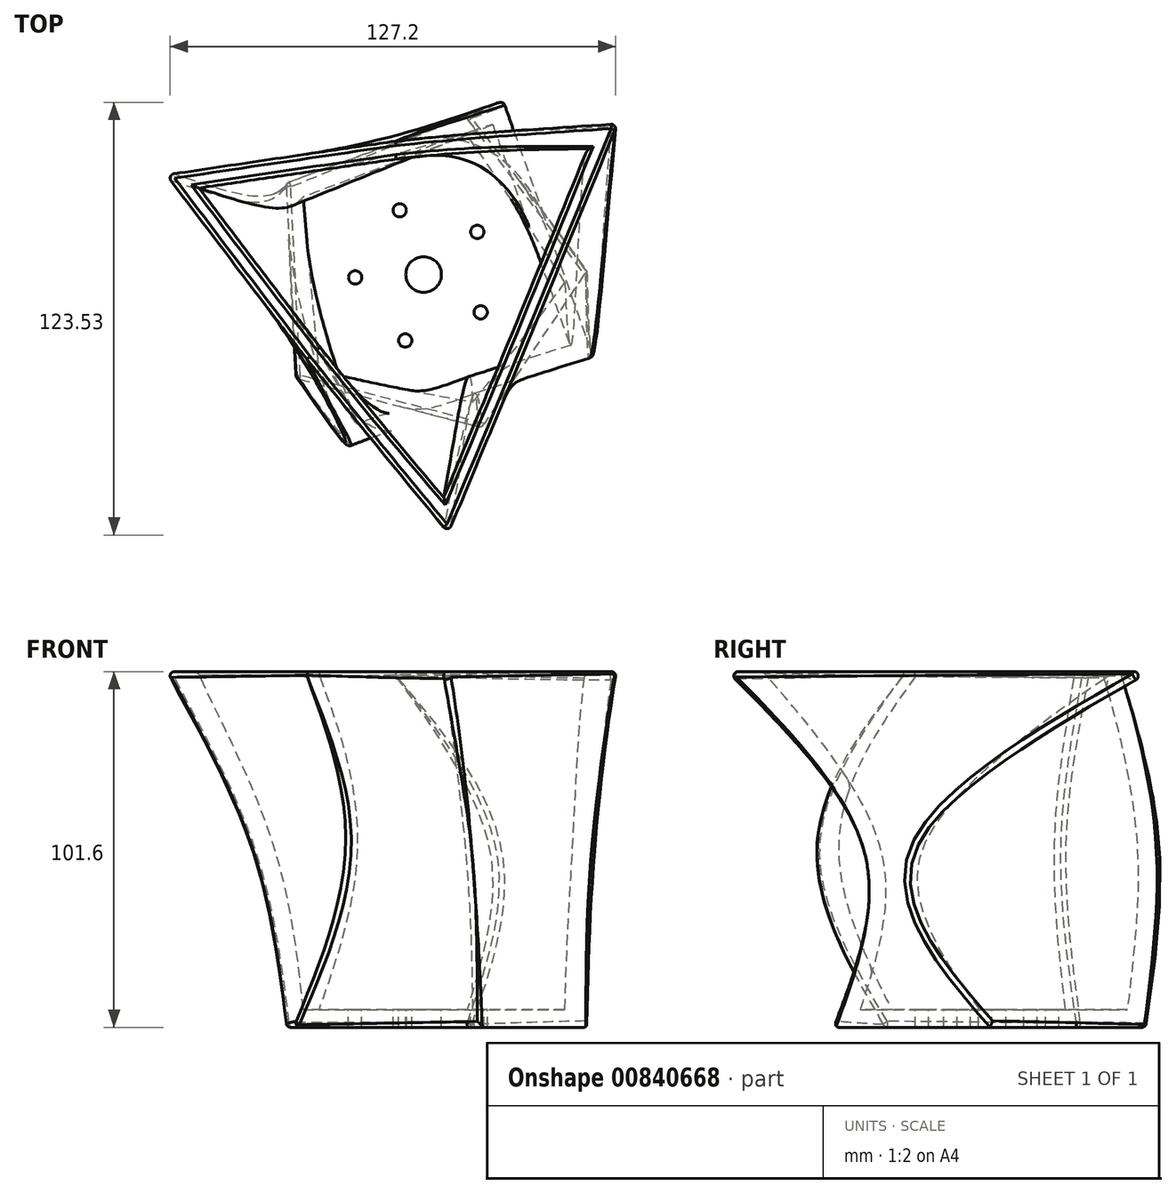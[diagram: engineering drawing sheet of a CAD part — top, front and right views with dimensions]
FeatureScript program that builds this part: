
annotation { "Feature Type Name" : "Feature", "Feature Type Description" : "" }
export const myFeature = defineFeature(function(context is Context, id is Id, definition is map)
    precondition{}
    {
        {
            var Q0;
            Q0=qCreatedBy(makeId("Top.planeOp"),FACE);
            var sketch = newSketch(context, id + "F0", { "sketchPlane" : qUnion([Q0])});
            skCircle(sketch, "E0.cCircle", {"center": v(0, 0) * mm, "radius": 38.1 * mm, "construction": true});
            skLineSegment(sketch, "E0.0", {"start": v(-39.1, 26.24) * mm, "end": v(12.87, 45.3) * mm});
            skLineSegment(sketch, "E0.1", {"start": v(12.87, 45.3) * mm, "end": v(47.06, 1.76) * mm});
            skLineSegment(sketch, "E0.2", {"start": v(47.06, 1.76) * mm, "end": v(16.21, -44.22) * mm});
            skLineSegment(sketch, "E0.3", {"start": v(16.21, -44.22) * mm, "end": v(-37.04, -29.08) * mm});
            skLineSegment(sketch, "E0.4", {"start": v(-37.04, -29.08) * mm, "end": v(-39.1, 26.24) * mm});
            skPoint(sketch, "E0.0.midPoint", {"position": v(-13.12, 35.77) * mm});
            skSolve(sketch);
        }
        {
            var Q0;
            Q0=qCreatedBy(makeId("Top.planeOp"),FACE);
            cPlane(context, id + "F1", {"entities" : qUnion([Q0]), "cplaneType" : CPlaneType.OFFSET, "offset" : 50.8 * mm, "width" : 152.4 * mm, "height" : 152.4 * mm});
        }
        {
            var Q0;
            Q0=qCreatedBy(id+"F1.planeOp",FACE);
            var sketch = newSketch(context, id + "F2", { "sketchPlane" : qUnion([Q0])});
            skCircle(sketch, "E1.cCircle", {"center": v(0, 0) * mm, "radius": 38.1 * mm, "construction": true});
            skLineSegment(sketch, "E1.0", {"start": v(-49.26, 21.84) * mm, "end": v(21.84, 49.26) * mm});
            skLineSegment(sketch, "E1.1", {"start": v(21.84, 49.26) * mm, "end": v(49.26, -21.84) * mm});
            skLineSegment(sketch, "E1.2", {"start": v(49.26, -21.84) * mm, "end": v(-21.84, -49.26) * mm});
            skLineSegment(sketch, "E1.3", {"start": v(-21.84, -49.26) * mm, "end": v(-49.26, 21.84) * mm});
            skPoint(sketch, "E1.0.midPoint", {"position": v(-13.71, 35.55) * mm});
            skSolve(sketch);
        }
        {
            var Q0;
            Q0=qCreatedBy(id+"F1.planeOp",FACE);
            cPlane(context, id + "F3", {"entities" : qUnion([Q0]), "cplaneType" : CPlaneType.OFFSET, "offset" : 50.8 * mm, "width" : 152.4 * mm, "height" : 152.4 * mm});
        }
        {
            var Q0;
            Q0=qCreatedBy(id+"F3.planeOp",FACE);
            var sketch = newSketch(context, id + "F4", { "sketchPlane" : qUnion([Q0])});
            skCircle(sketch, "E2.cCircle", {"center": v(-3.69, 0) * mm, "radius": 38.1 * mm, "construction": true});
            skLineSegment(sketch, "E2.0", {"start": v(-74.27, 28.73) * mm, "end": v(56.48, 46.76) * mm});
            skLineSegment(sketch, "E2.1", {"start": v(56.48, 46.76) * mm, "end": v(6.72, -75.49) * mm});
            skLineSegment(sketch, "E2.2", {"start": v(6.72, -75.49) * mm, "end": v(-74.27, 28.73) * mm});
            skPoint(sketch, "E2.0.midPoint", {"position": v(-8.9, 37.74) * mm});
            skSolve(sketch);
        }
        {
            var Q0;
            Q0=makeQuery(id+"F0.imprint","IMPRINT",FACE,{"disambiguationData":[TD([[makeQuery(id+"F0.imprint","IMPRINT",EDGE,{"derivedFrom":sQuery(id+"F0.wireOp",EDGE,"E0.0")}),-1.0]])]});
            var Q1;
            Q1=makeQuery(id+"F2.imprint","IMPRINT",FACE,{"disambiguationData":[TD([[makeQuery(id+"F2.imprint","IMPRINT",EDGE,{"derivedFrom":sQuery(id+"F2.wireOp",EDGE,"E1.0")}),-1.0]])]});
            var Q2;
            Q2=makeQuery(id+"F4.imprint","IMPRINT",FACE,{"disambiguationData":[TD([[makeQuery(id+"F4.imprint","IMPRINT",EDGE,{"derivedFrom":sQuery(id+"F4.wireOp",EDGE,"E2.0")}),-1.0]])]});
            loft(context, id + "F5", {"sheetProfilesArray" : [{ "sheetProfileEntities" : qUnion([Q0]) }, { "sheetProfileEntities" : qUnion([Q1]) }, { "sheetProfileEntities" : qUnion([Q2]) }]});
        }
        {
            var Q0;
            Q0=makeQuery(id+"F5.opLoft","CAP_FACE",FACE,{"disambiguationData":[OSD([makeQuery(id+"F4.imprint","IMPRINT",FACE,{"disambiguationData":[TD([[makeQuery(id+"F4.imprint","IMPRINT",EDGE,{"derivedFrom":sQuery(id+"F4.wireOp",EDGE,"E2.0")}),-1.0]])]})])],"isStart":true});
            shell(context, id + "F6", {"entities" : qUnion([Q0]), "thickness" : 5.08 * mm});
        }
        {
            var Q0;
            Q0=makeQuery(id+"F5.opLoft","CAP_FACE",FACE,{"disambiguationData":[OSD([makeQuery(id+"F4.imprint","IMPRINT",FACE,{"disambiguationData":[TD([[makeQuery(id+"F4.imprint","IMPRINT",EDGE,{"derivedFrom":sQuery(id+"F4.wireOp",EDGE,"E2.0")}),-1.0]])]})])],"isStart":true});
            var Q1;
            Q1=makeQuery(id+"F5.opLoft","SWEPT_FACE",FACE,{"disambiguationData":[OSD([sQuery(id+"F0.wireOp",EDGE,"E0.0"),sQuery(id+"F0.wireOp",EDGE,"E0.1"),sQuery(id+"F0.wireOp",EDGE,"E0.2"),sQuery(id+"F2.wireOp",EDGE,"E1.0"),sQuery(id+"F2.wireOp",EDGE,"E1.1"),sQuery(id+"F2.wireOp",EDGE,"E1.2"),sQuery(id+"F4.wireOp",EDGE,"E2.0"),sQuery(id+"F4.wireOp",EDGE,"E2.1"),sQuery(id+"F4.wireOp",EDGE,"E2.2")])]});
            var Q2;
            Q2=makeQuery(id+"F5.opLoft","SWEPT_FACE",FACE,{"disambiguationData":[OSD([sQuery(id+"F0.wireOp",EDGE,"E0.1"),sQuery(id+"F0.wireOp",EDGE,"E0.2"),sQuery(id+"F0.wireOp",EDGE,"E0.3"),sQuery(id+"F0.wireOp",EDGE,"E0.4"),sQuery(id+"F2.wireOp",EDGE,"E1.1"),sQuery(id+"F2.wireOp",EDGE,"E1.2"),sQuery(id+"F2.wireOp",EDGE,"E1.3"),sQuery(id+"F4.wireOp",EDGE,"E2.1"),sQuery(id+"F4.wireOp",EDGE,"E2.2")])]});
            var Q3;
            Q3=makeQuery(id+"F5.opLoft","SWEPT_FACE",FACE,{"disambiguationData":[OSD([sQuery(id+"F0.wireOp",EDGE,"E0.0"),sQuery(id+"F0.wireOp",EDGE,"E0.2"),sQuery(id+"F0.wireOp",EDGE,"E0.3"),sQuery(id+"F0.wireOp",EDGE,"E0.4"),sQuery(id+"F2.wireOp",EDGE,"E1.2"),sQuery(id+"F2.wireOp",EDGE,"E1.3"),sQuery(id+"F4.wireOp",EDGE,"E2.2")])]});
            var Q4;
            Q4=makeQuery(id+"F5.opLoft","SWEPT_FACE",FACE,{"disambiguationData":[OSD([sQuery(id+"F0.wireOp",EDGE,"E0.0"),sQuery(id+"F0.wireOp",EDGE,"E0.1"),sQuery(id+"F0.wireOp",EDGE,"E0.4"),sQuery(id+"F2.wireOp",EDGE,"E1.0"),sQuery(id+"F2.wireOp",EDGE,"E1.1"),sQuery(id+"F2.wireOp",EDGE,"E1.3"),sQuery(id+"F4.wireOp",EDGE,"E2.0"),sQuery(id+"F4.wireOp",EDGE,"E2.1"),sQuery(id+"F4.wireOp",EDGE,"E2.2")])]});
            var Q5;
            Q5=makeQuery(id+"F5.opLoft","MID_CAP_EDGE",EDGE,{"disambiguationData":[OSD([sQuery(id+"F0.wireOp",EDGE,"E0.0"),sQuery(id+"F0.wireOp",EDGE,"E0.3"),sQuery(id+"F0.wireOp",EDGE,"E0.4")])],"capPos":0.0});
            fillet(context, id + "F7", {"entities" : qUnion([Q0, Q1, Q2, Q3, Q4, Q5]), "radius" : 1.27 * mm, "tangentPropagation" : true, "allowEdgeOverflow" : false});
        }
        {
            var Q0;
            Q0=makeQuery(id+"F6.opShell","OFFSET_FACE",FACE,{"disambiguationData":[OSD([makeQuery(id+"F0.imprint","IMPRINT",FACE,{"disambiguationData":[TD([[makeQuery(id+"F0.imprint","IMPRINT",EDGE,{"derivedFrom":sQuery(id+"F0.wireOp",EDGE,"E0.0")}),-1.0]])]})])]});
            var sketch = newSketch(context, id + "F8", { "sketchPlane" : qUnion([Q0])});
            skCircle(sketch, "E3", {"center": v(-6.83, 18.33) * mm, "radius": 1.9 * mm});
            skCircle(sketch, "E4.1.0", {"center": v(-19.54, -0.83) * mm, "radius": 1.9 * mm});
            skCircle(sketch, "E4.2.0", {"center": v(-5.25, -18.84) * mm, "radius": 1.9 * mm});
            skCircle(sketch, "E4.3.0", {"center": v(16.3, -10.81) * mm, "radius": 1.9 * mm});
            skCircle(sketch, "E4.4.0", {"center": v(15.32, 12.16) * mm, "radius": 1.9 * mm});
            skPoint(sketch, "E4.center", {"position": v(0, 0) * mm});
            skSolve(sketch);
        }
        {
            var Q0;
            Q0 = qSketchRegion(id + "F8", true);
            extrude(context, id + "F9", {"entities" : qUnion([Q0]), "operationType" : NewBodyOperationType.REMOVE, "endBound" : BoundingType.THROUGH_ALL, "oppositeDirection" : true, "depth" : 25.4 * mm, "offsetDistance" : 25.4 * mm});
        }
        {
            var Q0;
            Q0=makeQuery(id+"F6.opShell","OFFSET_FACE",FACE,{"disambiguationData":[OSD([makeQuery(id+"F0.imprint","IMPRINT",FACE,{"disambiguationData":[TD([[makeQuery(id+"F0.imprint","IMPRINT",EDGE,{"derivedFrom":sQuery(id+"F0.wireOp",EDGE,"E0.0")}),-1.0]])]})])]});
            var sketch = newSketch(context, id + "F10", { "sketchPlane" : qUnion([Q0])});
            skCircle(sketch, "E5", {"center": v(0, 0) * mm, "radius": 5.08 * mm});
            skSolve(sketch);
        }
        {
            var Q0;
            Q0 = qSketchRegion(id + "F10", true);
            extrude(context, id + "F11", {"entities" : qUnion([Q0]), "operationType" : NewBodyOperationType.REMOVE, "endBound" : BoundingType.THROUGH_ALL, "oppositeDirection" : true, "depth" : 25.4 * mm, "offsetDistance" : 25.4 * mm});
        }
    });
